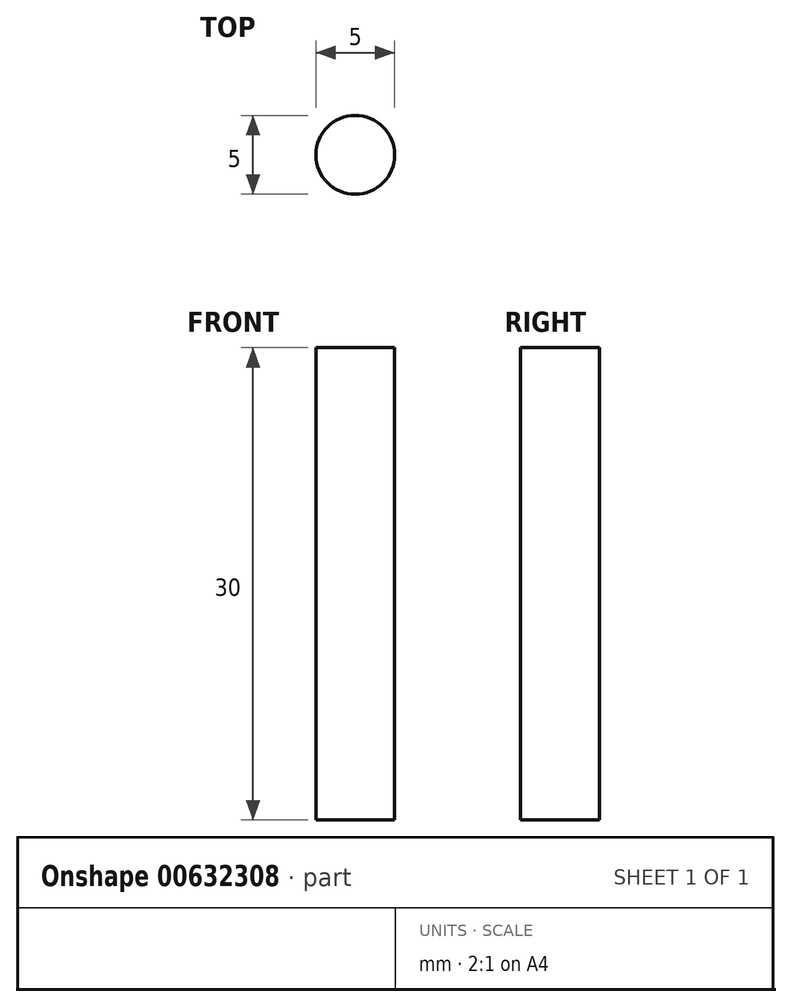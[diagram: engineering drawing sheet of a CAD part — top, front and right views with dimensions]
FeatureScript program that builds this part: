
annotation { "Feature Type Name" : "Feature", "Feature Type Description" : "" }
export const myFeature = defineFeature(function(context is Context, id is Id, definition is map)
    precondition{}
    {
        {
            var Q0;
            Q0=qCreatedBy(makeId("Top.planeOp"),FACE);
            var sketch = newSketch(context, id + "F0", { "sketchPlane" : qUnion([Q0])});
            skCircle(sketch, "E0", {"center": v(0, 0) * mm, "radius": 2.5 * mm});
            skSolve(sketch);
        }
        {
            var Q0;
            Q0=makeQuery(id+"F0.imprint","IMPRINT",FACE,{"disambiguationData":[TD([[makeQuery(id+"F0.imprint","IMPRINT",EDGE,{"derivedFrom":sQuery(id+"F0.wireOp",EDGE,"E0")}),1.0]])]});
            extrude(context, id + "F1", {"entities" : qUnion([Q0]), "depth" : 30 * mm, "offsetDistance" : 25 * mm});
        }
    });
